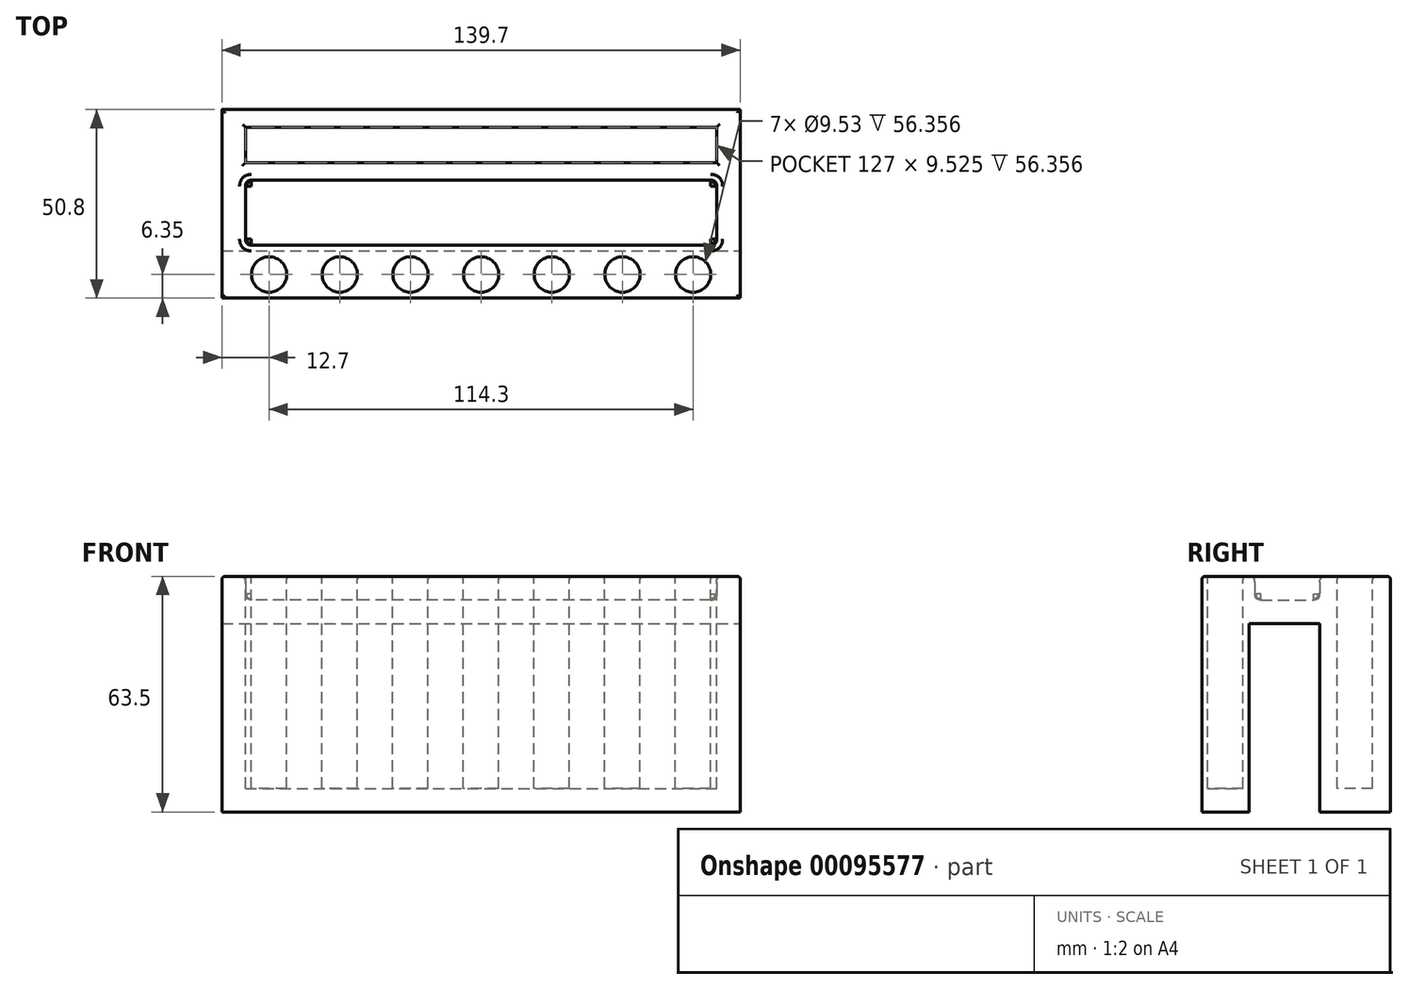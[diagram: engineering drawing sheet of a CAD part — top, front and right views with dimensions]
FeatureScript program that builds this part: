
annotation { "Feature Type Name" : "Feature", "Feature Type Description" : "" }
export const myFeature = defineFeature(function(context is Context, id is Id, definition is map)
    precondition{}
    {
        {
            var Q0;
            Q0=qCreatedBy(makeId("Top.planeOp"),FACE);
            var sketch = newSketch(context, id + "F0", { "sketchPlane" : qUnion([Q0])});
            skLineSegment(sketch, "E0.bottom", {"start": v(0, 0) * mm, "end": v(139.7, 0) * mm});
            skLineSegment(sketch, "E0.top", {"start": v(0, 50.8) * mm, "end": v(139.7, 50.8) * mm});
            skLineSegment(sketch, "E0.left", {"start": v(0, 0) * mm, "end": v(0, 50.8) * mm});
            skLineSegment(sketch, "E0.right", {"start": v(139.7, 0) * mm, "end": v(139.7, 50.8) * mm});
            skSolve(sketch);
        }
        {
            var Q0;
            Q0 = qSketchRegion(id + "F0", true);
            extrude(context, id + "F1", {"entities" : qUnion([Q0]), "depth" : 63.5 * mm});
        }
        {
            var Q0;
            Q0=makeQuery(id+"F1.opExtrude","CAP_FACE",FACE,{"disambiguationData":[OSD([sQuery(id+"F0.wireOp",EDGE,"E0.bottom"),sQuery(id+"F0.wireOp",EDGE,"E0.top"),sQuery(id+"F0.wireOp",EDGE,"E0.left"),sQuery(id+"F0.wireOp",EDGE,"E0.right")])],"isStart":true});
            var sketch = newSketch(context, id + "F2", { "sketchPlane" : qUnion([Q0])});
            skLineSegment(sketch, "E1", {"start": v(0, 0) * mm, "end": v(0, -12.7) * mm});
            skLineSegment(sketch, "E2", {"start": v(0, -12.7) * mm, "end": v(0, -31.75) * mm});
            skLineSegment(sketch, "E3", {"start": v(0, -31.75) * mm, "end": v(0, -50.8) * mm});
            skLineSegment(sketch, "E4.bottom", {"start": v(0, -12.7) * mm, "end": v(139.7, -12.7) * mm});
            skLineSegment(sketch, "E4.top", {"start": v(0, -31.75) * mm, "end": v(139.7, -31.75) * mm});
            skLineSegment(sketch, "E4.right", {"start": v(139.7, -12.7) * mm, "end": v(139.7, -31.75) * mm});
            skSolve(sketch);
        }
        {
            var Q0;
            Q0 = qSketchRegion(id + "F2", true);
            extrude(context, id + "F3", {"entities" : qUnion([Q0]), "operationType" : NewBodyOperationType.REMOVE, "oppositeDirection" : true, "depth" : 50.8 * mm});
        }
        {
            var Q0;
            Q0=makeQuery(id+"F1.opExtrude","CAP_FACE",FACE,{"disambiguationData":[OSD([sQuery(id+"F0.wireOp",EDGE,"E0.bottom"),sQuery(id+"F0.wireOp",EDGE,"E0.top"),sQuery(id+"F0.wireOp",EDGE,"E0.left"),sQuery(id+"F0.wireOp",EDGE,"E0.right")])],"isStart":false});
            var sketch = newSketch(context, id + "F4", { "sketchPlane" : qUnion([Q0])});
            skLineSegment(sketch, "E5", {"start": v(0, 0) * mm, "end": v(0, 6.35) * mm});
            skLineSegment(sketch, "E6", {"start": v(0, 6.35) * mm, "end": v(0, 12.7) * mm});
            skLineSegment(sketch, "E7", {"start": v(0, 12.7) * mm, "end": v(0, 31.75) * mm});
            skLineSegment(sketch, "E8", {"start": v(0, 31.75) * mm, "end": v(0, 50.8) * mm});
            skCircle(sketch, "E9", {"center": v(12.7, 6.35) * mm, "radius": 4.76 * mm});
            skCircle(sketch, "E10.1.0.0", {"center": v(31.75, 6.35) * mm, "radius": 4.76 * mm});
            skCircle(sketch, "E10.2.0.0", {"center": v(50.8, 6.35) * mm, "radius": 4.76 * mm});
            skCircle(sketch, "E10.3.0.0", {"center": v(69.85, 6.35) * mm, "radius": 4.76 * mm});
            skCircle(sketch, "E10.4.0.0", {"center": v(88.9, 6.35) * mm, "radius": 4.76 * mm});
            skCircle(sketch, "E10.5.0.0", {"center": v(107.95, 6.35) * mm, "radius": 4.76 * mm});
            skCircle(sketch, "E10.6.0.0", {"center": v(127, 6.35) * mm, "radius": 4.76 * mm});
            skLineSegment(sketch, "E10.direction1", {"start": v(12.7, 6.35) * mm, "end": v(31.75, 6.35) * mm, "construction": true});
            skLineSegment(sketch, "E11", {"start": v(0, 50.8) * mm, "end": v(6.35, 50.8) * mm});
            skLineSegment(sketch, "E12", {"start": v(6.35, 50.8) * mm, "end": v(6.35, 46.04) * mm});
            skLineSegment(sketch, "E13.bottom", {"start": v(6.35, 46.04) * mm, "end": v(133.35, 46.04) * mm});
            skLineSegment(sketch, "E13.top", {"start": v(6.35, 36.51) * mm, "end": v(133.35, 36.51) * mm});
            skLineSegment(sketch, "E13.left", {"start": v(6.35, 46.04) * mm, "end": v(6.35, 36.51) * mm});
            skLineSegment(sketch, "E13.right", {"start": v(133.35, 46.04) * mm, "end": v(133.35, 36.51) * mm});
            skLineSegment(sketch, "E14", {"start": v(0, 31.75) * mm, "end": v(6.35, 31.75) * mm});
            skLineSegment(sketch, "E15", {"start": v(6.35, 31.75) * mm, "end": v(6.35, 14.29) * mm});
            skLineSegment(sketch, "E16", {"start": v(6.35, 14.29) * mm, "end": v(133.35, 14.29) * mm});
            skLineSegment(sketch, "E17", {"start": v(133.35, 14.29) * mm, "end": v(133.35, 31.75) * mm});
            skLineSegment(sketch, "E18", {"start": v(133.35, 31.75) * mm, "end": v(6.35, 31.75) * mm});
            skSolve(sketch);
        }
        {
            var Q0;
            Q0=makeQuery(id+"F4.imprint","IMPRINT",FACE,{"disambiguationData":[TD([[makeQuery(id+"F4.imprint","IMPRINT",EDGE,{"derivedFrom":sQuery(id+"F4.wireOp",EDGE,"E9")}),1.0]])]});
            var Q1;
            Q1=makeQuery(id+"F4.imprint","IMPRINT",FACE,{"disambiguationData":[TD([[makeQuery(id+"F4.imprint","IMPRINT",EDGE,{"derivedFrom":sQuery(id+"F4.wireOp",EDGE,"E10.1.0.0")}),1.0]])]});
            var Q2;
            Q2=makeQuery(id+"F4.imprint","IMPRINT",FACE,{"disambiguationData":[TD([[makeQuery(id+"F4.imprint","IMPRINT",EDGE,{"derivedFrom":sQuery(id+"F4.wireOp",EDGE,"E10.2.0.0")}),1.0]])]});
            var Q3;
            Q3=makeQuery(id+"F4.imprint","IMPRINT",FACE,{"disambiguationData":[TD([[makeQuery(id+"F4.imprint","IMPRINT",EDGE,{"derivedFrom":sQuery(id+"F4.wireOp",EDGE,"E10.3.0.0")}),1.0]])]});
            var Q4;
            Q4=makeQuery(id+"F4.imprint","IMPRINT",FACE,{"disambiguationData":[TD([[makeQuery(id+"F4.imprint","IMPRINT",EDGE,{"derivedFrom":sQuery(id+"F4.wireOp",EDGE,"E10.4.0.0")}),1.0]])]});
            var Q5;
            Q5=makeQuery(id+"F4.imprint","IMPRINT",FACE,{"disambiguationData":[TD([[makeQuery(id+"F4.imprint","IMPRINT",EDGE,{"derivedFrom":sQuery(id+"F4.wireOp",EDGE,"E10.5.0.0")}),1.0]])]});
            var Q6;
            Q6=makeQuery(id+"F4.imprint","IMPRINT",FACE,{"disambiguationData":[TD([[makeQuery(id+"F4.imprint","IMPRINT",EDGE,{"derivedFrom":sQuery(id+"F4.wireOp",EDGE,"E10.6.0.0")}),1.0]])]});
            var Q7;
            Q7=makeQuery(id+"F4.imprint","IMPRINT",FACE,{"disambiguationData":[TD([[makeQuery(id+"F4.imprint","IMPRINT",EDGE,{"derivedFrom":sQuery(id+"F4.wireOp",EDGE,"E13.bottom")}),-1.0]])]});
            extrude(context, id + "F5", {"entities" : qUnion([Q0, Q1, Q2, Q3, Q4, Q5, Q6, Q7]), "operationType" : NewBodyOperationType.REMOVE, "oppositeDirection" : true, "depth" : 57.15 * mm});
        }
        {
            var Q0;
            Q0=makeQuery(id+"F4.imprint","IMPRINT",FACE,{"disambiguationData":[TD([[makeQuery(id+"F4.imprint","IMPRINT",EDGE,{"derivedFrom":sQuery(id+"F4.wireOp",EDGE,"E15")}),1.0]])]});
            extrude(context, id + "F6", {"entities" : qUnion([Q0]), "operationType" : NewBodyOperationType.REMOVE, "oppositeDirection" : true, "depth" : 6.35 * mm});
        }
        {
            var Q0;
            Q0=makeQuery(id+"F6.boolean.opBoolean","COPY",FACE,{"derivedFrom":makeQuery(id+"F6.opExtrude","SWEPT_FACE",FACE,{"disambiguationData":[OSD([sQuery(id+"F4.wireOp",EDGE,"E18")])]})});
            var Q1;
            Q1=makeQuery(id+"F6.boolean.opBoolean","COPY",FACE,{"derivedFrom":makeQuery(id+"F6.opExtrude","CAP_FACE",FACE,{"disambiguationData":[OSD([sQuery(id+"F4.wireOp",EDGE,"E15"),sQuery(id+"F4.wireOp",EDGE,"E16"),sQuery(id+"F4.wireOp",EDGE,"E17"),sQuery(id+"F4.wireOp",EDGE,"E18")])],"isStart":false})});
            var Q2;
            Q2=makeQuery(id+"F6.boolean.opBoolean","COPY",FACE,{"derivedFrom":makeQuery(id+"F6.opExtrude","SWEPT_FACE",FACE,{"disambiguationData":[OSD([sQuery(id+"F4.wireOp",EDGE,"E15")])]})});
            var Q3;
            Q3=makeQuery(id+"F6.boolean.opBoolean","COPY",FACE,{"derivedFrom":makeQuery(id+"F6.opExtrude","SWEPT_FACE",FACE,{"disambiguationData":[OSD([sQuery(id+"F4.wireOp",EDGE,"E17")])]})});
            var Q4;
            Q4=makeQuery(id+"F6.boolean.opBoolean","COPY",FACE,{"derivedFrom":makeQuery(id+"F6.opExtrude","SWEPT_FACE",FACE,{"disambiguationData":[OSD([sQuery(id+"F4.wireOp",EDGE,"E16")])]})});
            fillet(context, id + "F7", {"entities" : qUnion([Q0, Q1, Q2, Q3, Q4]), "radius" : 1.59 * mm, "tangentPropagation" : true, "rho" : 0.5, "crossSection" : FilletCrossSection.CONIC, "allowEdgeOverflow" : false});
        }
        {
            var Q0;
            Q0=makeQuery(id+"F1.opExtrude","CAP_FACE",FACE,{"disambiguationData":[OSD([sQuery(id+"F0.wireOp",EDGE,"E0.bottom"),sQuery(id+"F0.wireOp",EDGE,"E0.top"),sQuery(id+"F0.wireOp",EDGE,"E0.left"),sQuery(id+"F0.wireOp",EDGE,"E0.right")])],"isStart":false});
            fillet(context, id + "F8", {"entities" : qUnion([Q0]), "radius" : 0.8 * mm, "tangentPropagation" : true, "allowEdgeOverflow" : false});
        }
    });
